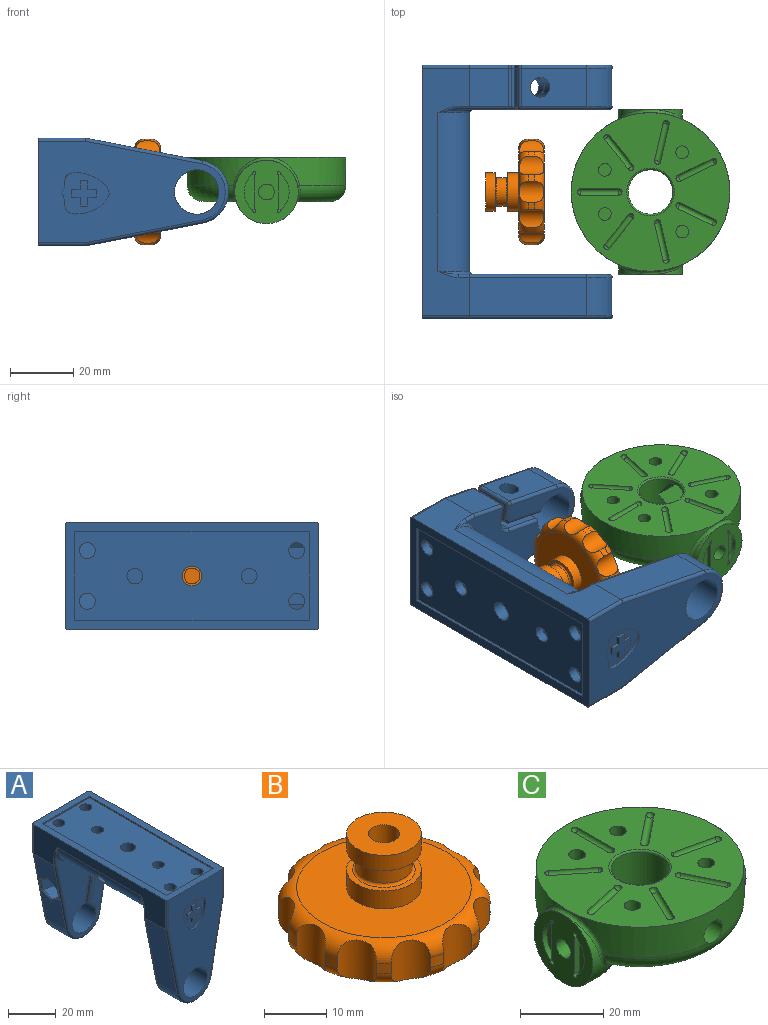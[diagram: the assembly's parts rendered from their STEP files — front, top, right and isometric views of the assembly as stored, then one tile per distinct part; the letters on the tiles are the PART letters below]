
ASSEMBLY  parts=3 mates=2
PART A: 167 faces, bbox 39.4x80x60.8 mm
  f0: plane 59x32mm, normal (0,-1,0), area 1187mm2, adj f6,f16,f97,f98,f99,f100,f101,f162
  f1: plane 36.91x12mm, normal (-0.98,0,-0.19), area 346.3mm2, adj f17,f18,f86,f104,f129,f130,f131,f132
  f2: plane 74x0.7mm, normal (-1,0,0), area 51.8mm2, adj f3,f5,f6,f35
  f3: plane 28x0.7mm, normal (0,1,0), area 19.6mm2, adj f2,f4,f6,f35
  f4: plane 74x0.7mm, normal (1,0,0), area 51.8mm2, adj f3,f5,f6,f35
  f5: plane 28x0.7mm, normal (0,-1,0), area 19.6mm2, adj f2,f4,f6,f35
  f6: plane 80x34mm, normal (0,0,1), area 647.1mm2, adj f0,f2,f3,f4,f5,f17,f19,f20
  f7: cylinder r=3.1mm len=6.2mm, axis (0,0,-1), area 83.8mm2, adj f31,f35
  f8: cylinder r=6.1mm len=12.2mm, axis (0,0,-1), area 378.3mm2, adj f22,f31,f32
  f9: plane 20.61x12mm, normal (0.98,0,-0.19), area 221.8mm2, adj f18,f29,f88,f107,f108
  f10: plane 12.37x12mm, normal (0.98,0,-0.19), area 151.2mm2, adj f19,f93,f123,f126
  f11: cylinder r=7mm len=14mm, axis (0,1,0), area 586.5mm2, adj f12,f20,f25,f28,f91,f96,f112,f120
  f12: plane 47.68x32mm, normal (0,-1,0), area 755.3mm2, adj f11,f79,f80,f81,f103,f104,f106,f108
  f13: plane 36.91x12mm, normal (-0.98,0,-0.19), area 451.2mm2, adj f14,f17,f98,f115
  f14: cylinder r=10mm len=19.63mm, axis (0,1,0), area 330.9mm2, adj f13,f15,f100,f117
  f15: plane 36.91x12mm, normal (0.98,0,-0.19), area 451.2mm2, adj f14,f19,f101,f119
  f16: cylinder r=7mm len=14mm, axis (0,1,0), area 615.8mm2, adj f0,f21
  f17: plane 78x15mm, normal (-1,0,0), area 639.6mm2, adj f1,f6,f13,f74,f85,f97,f102,f103
  f18: cylinder r=10mm len=19.63mm, axis (0,1,0), area 330.9mm2, adj f1,f9,f87,f106
  f19: plane 78x15mm, normal (1,0,0), area 639.6mm2, adj f6,f10,f15,f73,f92,f99,f116,f118
  f20: plane 59x32mm, normal (0,1,0), area 1095.5mm2, adj f6,f11,f85,f86,f87,f88,f89,f90
  f21: plane 47.68x32mm, normal (0,1,0), area 846.9mm2, adj f16,f82,f83,f84,f114,f115,f117,f118
  f22: plane 50x14mm, normal (0,0,-1), area 583.1mm2, adj f8,f73,f74,f80,f83
  f23: plane 12x4.91mm, normal (-0.19,0,-0.98), area 60mm2, adj f24,f94,f123,f124
  f24: cylinder r=4mm len=12mm, axis (0,1,0), area 75.4mm2, adj f23,f25,f95,f122
  f25: plane 12.76x12mm, normal (0.98,0,-0.19), area 125.8mm2, adj f11,f24,f30,f96,f120
  f26: cylinder r=2mm len=12mm, axis (0,1,0), area 37.7mm2, adj f27,f28,f90,f111
  f27: plane 12x4.91mm, normal (0.19,0,0.98), area 60mm2, adj f26,f89,f107,f110
  f28: plane 13.05x12mm, normal (-0.98,0,0.19), area 129.3mm2, adj f11,f26,f29,f91,f112
  f29: cylinder r=3.1mm len=9.04mm, axis (0.98,0,-0.19), area 155.8mm2, adj f9,f28
  f30: cylinder r=3.1mm len=9.04mm, axis (0.98,0,-0.19), area 155.8mm2, adj f25,f72
  f31: plane 12.2x12.2mm, normal (0,0,-1), area 86.7mm2, adj f7,f8
  f32: cylinder r=1.25mm len=4.03mm, axis (-1,0,0), area 31.1mm2, adj f8,f33
  f33: plane 6x6mm, normal (-1,0,0), area 23.4mm2, adj f32,f34
  f34: cylinder r=3mm len=6.8mm, axis (-1,0,0), area 99.7mm2, adj f33,f74
  f35: plane 74x28mm, normal (0,0,1), area 1924mm2, adj f2,f3,f4,f5,f7,f36,f37,f38
  f36: cylinder r=2.5mm len=5mm, axis (0,0,1), area 47.1mm2, adj f35,f39
  f37: cylinder r=2.5mm len=5mm, axis (0,0,1), area 47.1mm2, adj f35,f39
  f38: cylinder r=2.5mm len=5mm, axis (0,0,1), area 47.1mm2, adj f35,f39
  f39: plane 35.5x28mm, normal (0,0,-1), area 808mm2, adj f36,f37,f38,f45,f46,f47,f48,f49
  f40: plane 9.85x8mm, normal (-0.98,0,0.19), area 80.2mm2, adj f41,f43,f48,f49
  f41: plane 25.12x8mm, normal (0.19,0,0.98), area 204.7mm2, adj f40,f42,f43,f48
  f42: plane 8x4.96mm, normal (0.98,0,0.19), area 40.4mm2, adj f41,f43,f47,f48
  f43: plane 28x19.85mm, normal (0,1,0), area 302.8mm2, adj f40,f41,f42,f44,f47,f49,f77,f78
  f44: plane 23.34x14mm, normal (0,0,1), area 294.2mm2, adj f43,f45,f46,f77,f78
  f45: plane 8.3x7.29mm, normal (0,1,0), area 50mm2, adj f39,f44,f46,f47,f78
  f46: cylinder r=9mm len=15.58mm, axis (0,0,1), area 167.1mm2, adj f39,f44,f45,f50,f77
  f47: plane 31x11.3mm, normal (1,0,0), area 120.3mm2, adj f39,f42,f43,f45,f48,f78
  f48: plane 28x21.15mm, normal (0,-1,0), area 514.1mm2, adj f39,f40,f41,f42,f47,f49
  f49: plane 35.5x11.3mm, normal (-1,0,0), area 126.2mm2, adj f39,f40,f43,f48,f50,f77
  f50: plane 8.04x5.13mm, normal (0,1,0), area 32.2mm2, adj f39,f46,f49,f77
  f51: cylinder r=2.5mm len=5mm, axis (0,0,1), area 47.1mm2, adj f35,f54
  f52: cylinder r=2.5mm len=5mm, axis (0,0,1), area 47.1mm2, adj f35,f54
  f53: cylinder r=2.5mm len=5mm, axis (0,0,1), area 47.1mm2, adj f35,f54
  f54: plane 35.5x28mm, normal (0,0,-1), area 808mm2, adj f51,f52,f53,f60,f61,f62,f63,f64
  f55: plane 35x28mm, normal (0,-1,0), area 683.4mm2, adj f56,f57,f58,f59,f64,f65,f75,f76
  f56: plane 25x8mm, normal (0.98,0,0.19), area 203.8mm2, adj f55,f57,f60,f64
  f57: plane 18.27x8mm, normal (0,0,1), area 146.1mm2, adj f55,f56,f58,f60
  f58: plane 25x8mm, normal (-0.98,0,0.19), area 203.8mm2, adj f55,f57,f60,f65
  f59: plane 23.34x14mm, normal (0,0,1), area 294.2mm2, adj f55,f61,f62,f75,f76
  f60: plane 36.3x28mm, normal (0,1,0), area 894.8mm2, adj f54,f56,f57,f58,f64,f65
  f61: plane 8.3x7.29mm, normal (0,-1,0), area 50mm2, adj f54,f59,f62,f64,f76
  f62: cylinder r=9mm len=15.58mm, axis (0,0,1), area 167.1mm2, adj f54,f59,f61,f63,f75
  f63: plane 8.04x5.13mm, normal (0,-1,0), area 32.2mm2, adj f54,f62,f65,f75
  f64: plane 31x11.3mm, normal (1,0,0), area 120.3mm2, adj f54,f55,f56,f60,f61,f76
  f65: plane 35.5x11.3mm, normal (-1,0,0), area 126.1mm2, adj f54,f55,f58,f60,f63,f75
  f66: plane 10.55x4.84mm, normal (-0.17,0.5,-0.85), area 56.4mm2, adj f67,f71,f72,f132,f134
  f67: plane 9.27x7.25mm, normal (0,1,0), area 46.1mm2, adj f66,f68,f72,f130,f132
  f68: plane 6.89x4.8mm, normal (0.17,0.5,0.85), area 35.8mm2, adj f67,f69,f72,f130
  f69: plane 6.89x4.8mm, normal (0.17,-0.5,0.85), area 35.8mm2, adj f68,f70,f72,f129
  f70: plane 9.27x7.25mm, normal (0,-1,0), area 46.1mm2, adj f69,f71,f72,f129,f131
  f71: plane 10.55x4.84mm, normal (-0.17,-0.5,-0.85), area 56.4mm2, adj f66,f70,f72,f131,f133
  f72: plane 10.88x9.6mm, normal (-0.98,0,0.19), area 49.6mm2, adj f30,f66,f67,f68,f69,f70,f71
  f73: cylinder r=10mm len=50mm, axis (0,-1,0), area 785.4mm2, adj f19,f22,f81,f84
  f74: cylinder r=10mm len=50mm, axis (0,1,0), area 751.6mm2, adj f17,f22,f34,f79,f82
  f75: cylinder r=7mm len=27.5mm, axis (0,1,0), area 297.6mm2, adj f55,f59,f62,f63,f65
  f76: cylinder r=7mm len=23mm, axis (0,-1,0), area 252.9mm2, adj f55,f59,f61,f64
  f77: cylinder r=7mm len=27.5mm, axis (0,1,0), area 297.6mm2, adj f43,f44,f46,f49,f50
  f78: cylinder r=7mm len=23mm, axis (0,-1,0), area 252.9mm2, adj f43,f44,f45,f47
  f79: torus R=11mm, axis (0,1,0), area 20mm2, adj f12,f74,f80,f102
  f80: cylinder r=1mm len=14mm, axis (1,0,0), area 22mm2, adj f12,f22,f79,f81
  f81: torus R=11mm, axis (0,1,0), area 20mm2, adj f12,f73,f80,f128
  f82: torus R=11mm, axis (0,1,0), area 20mm2, adj f21,f74,f83,f113
  f83: cylinder r=1mm len=14mm, axis (-1,0,0), area 22mm2, adj f21,f22,f82,f84
  f84: torus R=11mm, axis (0,1,0), area 20mm2, adj f21,f73,f83,f116
  f85: cylinder r=1mm len=15mm, axis (0,0,-1), area 23.5mm2, adj f6,f17,f20,f86
  f86: cylinder r=1mm len=37.1mm, axis (0.19,0,-0.98), area 59mm2, adj f1,f20,f85,f87
  f87: torus R=9mm, axis (0,-1,0), area 41.7mm2, adj f18,f20,f86,f88
  f88: cylinder r=1mm len=20.8mm, axis (0.19,0,0.98), area 33mm2, adj f9,f20,f87,f105
  f89: cylinder r=1mm len=5.1mm, axis (-0.98,0,0.19), area 7.9mm2, adj f20,f27,f90,f105
  f90: torus R=1mm, axis (0,-1,0), area 4mm2, adj f20,f26,f89,f91
  f91: cylinder r=1mm len=13.61mm, axis (-0.19,0,-0.98), area 21.1mm2, adj f11,f20,f28,f90
  f92: cylinder r=1mm len=15mm, axis (0,0,1), area 23.5mm2, adj f6,f19,f20,f93
  f93: cylinder r=1mm len=12.56mm, axis (0.19,0,0.98), area 19.7mm2, adj f10,f20,f92,f121
  f94: cylinder r=1mm len=5.1mm, axis (0.98,0,-0.19), area 7.9mm2, adj f20,f23,f95,f121
  f95: torus R=5mm, axis (0,-1,0), area 10.8mm2, adj f20,f24,f94,f96
  f96: cylinder r=1mm len=13.02mm, axis (0.19,0,0.98), area 20.5mm2, adj f11,f20,f25,f95
  f97: cylinder r=1mm len=15mm, axis (0,0,1), area 23.5mm2, adj f0,f6,f17,f98
  f98: cylinder r=1mm len=37.1mm, axis (-0.19,0,0.98), area 59mm2, adj f0,f13,f97,f100
  f99: cylinder r=1mm len=15mm, axis (0,0,-1), area 23.5mm2, adj f0,f6,f19,f101
  f100: torus R=9mm, axis (0,-1,0), area 41.7mm2, adj f0,f14,f98,f101
  f101: cylinder r=1mm len=37.1mm, axis (-0.19,0,-0.98), area 59mm2, adj f0,f15,f99,f100
  f102: bspline ~6.59x2mm, area 5mm2, adj f17,f79,f103
  f103: cylinder r=1mm len=3.68mm, axis (0,0,1), area 5.7mm2, adj f12,f17,f102,f104
  f104: cylinder r=1mm len=37.1mm, axis (-0.19,0,0.98), area 59mm2, adj f1,f12,f103,f106
  f105: sphere r=1mm, area 1.5mm2, adj f88,f89,f107
  f106: torus R=9mm, axis (0,1,0), area 41.7mm2, adj f12,f18,f104,f108
  f107: cylinder r=1mm len=12mm, axis (0,-1,0), area 18.8mm2, adj f9,f27,f105,f109
  f108: cylinder r=1mm len=20.8mm, axis (-0.19,0,-0.98), area 33mm2, adj f9,f12,f106,f109
  f109: sphere r=1mm, area 1.6mm2, adj f107,f108,f110
  f110: cylinder r=1mm len=5.1mm, axis (-0.98,0,0.19), area 7.9mm2, adj f12,f27,f109,f111
  f111: torus R=1mm, axis (0,1,0), area 4mm2, adj f12,f26,f110,f112
  f112: cylinder r=1mm len=13.61mm, axis (-0.19,0,-0.98), area 21.1mm2, adj f11,f12,f28,f111
  f113: bspline ~6.59x2mm, area 5mm2, adj f17,f82,f114
  f114: cylinder r=1mm len=3.68mm, axis (0,0,1), area 5.7mm2, adj f17,f21,f113,f115
  f115: cylinder r=1mm len=37.1mm, axis (0.19,0,-0.98), area 59mm2, adj f13,f21,f114,f117
  f116: bspline ~6.59x2mm, area 5mm2, adj f19,f84,f118
  f117: torus R=9mm, axis (0,1,0), area 41.7mm2, adj f14,f21,f115,f119
  f118: cylinder r=1mm len=3.68mm, axis (0,0,1), area 5.7mm2, adj f19,f21,f116,f119
  f119: cylinder r=1mm len=37.1mm, axis (0.19,0,0.98), area 59mm2, adj f15,f21,f117,f118
  f120: cylinder r=1mm len=13.02mm, axis (0.19,0,0.98), area 20.5mm2, adj f11,f12,f25,f122
  f121: sphere r=1mm, area 1.6mm2, adj f93,f94,f123
  f122: torus R=5mm, axis (0,1,0), area 10.8mm2, adj f12,f24,f120,f124
  f123: cylinder r=1mm len=12mm, axis (0,1,0), area 18.8mm2, adj f10,f23,f121,f125
  f124: cylinder r=1mm len=5.1mm, axis (0.98,0,-0.19), area 7.9mm2, adj f12,f23,f122,f125
  f125: sphere r=1mm, area 1.6mm2, adj f123,f124,f126
  f126: cylinder r=1mm len=12.56mm, axis (-0.19,0,-0.98), area 19.7mm2, adj f10,f12,f125,f127
  f127: cylinder r=1mm len=3.68mm, axis (0,0,1), area 5.7mm2, adj f12,f19,f126,f128
  f128: bspline ~6.59x2mm, area 5mm2, adj f19,f81,f127
  f129: cylinder r=0.5mm len=5.56mm, axis (-0.1,0.85,0.52), area 5.6mm2, adj f1,f69,f70,f130,f131
  f130: cylinder r=0.5mm len=5.56mm, axis (0.1,0.85,-0.52), area 5.6mm2, adj f1,f67,f68,f129,f132
  f131: cylinder r=0.5mm len=6.58mm, axis (-0.19,0,0.98), area 4.9mm2, adj f1,f70,f71,f129,f133
  f132: cylinder r=0.5mm len=6.58mm, axis (0.19,0,-0.98), area 4.9mm2, adj f1,f66,f67,f130,f134
  f133: cylinder r=0.5mm len=5.55mm, axis (-0.1,-0.85,0.52), area 3.7mm2, adj f1,f71,f131,f134
  f134: cylinder r=0.5mm len=5.55mm, axis (0.1,-0.85,-0.52), area 3.7mm2, adj f1,f66,f132,f133
  f135: extruded ~15.03x6.52mm, area 22.3mm2, adj f20,f148,f149
  f136: plane 2.8x1mm, normal (-1,0,0), area 2.8mm2, adj f137,f147,f149,f150
  f137: plane 2.4x1mm, normal (0,0,-1), area 2.4mm2, adj f136,f138,f149,f150
  f138: plane 2.8x1mm, normal (1,0,0), area 2.8mm2, adj f137,f139,f149,f150
  f139: plane 2.8x1mm, normal (0,0,-1), area 2.8mm2, adj f138,f140,f149,f150
  f140: plane 2.4x1mm, normal (1,0,0), area 2.4mm2, adj f139,f141,f149,f150
  f141: plane 2.8x1mm, normal (0,0,1), area 2.8mm2, adj f140,f142,f149,f150
  f142: plane 2.8x1mm, normal (1,0,0), area 2.8mm2, adj f141,f143,f149,f150
  f143: plane 2.4x1mm, normal (0,0,1), area 2.4mm2, adj f142,f144,f149,f150
  f144: plane 2.8x1mm, normal (-1,0,0), area 2.8mm2, adj f143,f145,f149,f150
  f145: plane 2.8x1mm, normal (0,0,1), area 2.8mm2, adj f144,f146,f149,f150
  f146: plane 2.4x1mm, normal (-1,0,0), area 2.4mm2, adj f145,f147,f149,f150
  f147: plane 2.8x1mm, normal (0,0,-1), area 2.8mm2, adj f136,f146,f149,f150
  f148: extruded ~15.03x6.52mm, area 22.3mm2, adj f20,f135,f149
  f149: plane 15.18x13.69mm, normal (0,1,0), area 114.1mm2, adj f135,f136,f137,f138,f139,f140,f141,f142
  f150: plane 8x8mm, normal (0,1,0), area 32.6mm2, adj f136,f137,f138,f139,f140,f141,f142,f143
  f151: plane 2.8x1mm, normal (1,0,0), area 2.8mm2, adj f152,f164,f165,f166
  f152: plane 2.4x1mm, normal (0,0,-1), area 2.4mm2, adj f151,f153,f165,f166
  f153: plane 2.8x1mm, normal (-1,0,0), area 2.8mm2, adj f152,f154,f165,f166
  f154: plane 2.8x1mm, normal (0,0,-1), area 2.8mm2, adj f153,f155,f165,f166
  f155: plane 2.4x1mm, normal (-1,0,0), area 2.4mm2, adj f154,f156,f165,f166
  f156: plane 2.8x1mm, normal (0,0,1), area 2.8mm2, adj f155,f157,f165,f166
  f157: plane 2.8x1mm, normal (-1,0,0), area 2.8mm2, adj f156,f158,f165,f166
  f158: plane 2.4x1mm, normal (0,0,1), area 2.4mm2, adj f157,f159,f165,f166
  f159: plane 2.8x1mm, normal (1,0,0), area 2.8mm2, adj f158,f160,f165,f166
  f160: plane 2.8x1mm, normal (0,0,1), area 2.8mm2, adj f159,f161,f165,f166
  f161: plane 2.4x1mm, normal (1,0,0), area 2.4mm2, adj f160,f164,f165,f166
  f162: extruded ~15.03x6.52mm, area 22.3mm2, adj f0,f163,f165
  f163: extruded ~15.03x6.52mm, area 22.3mm2, adj f0,f162,f165
  f164: plane 2.8x1mm, normal (0,0,-1), area 2.8mm2, adj f151,f161,f165,f166
  f165: plane 15.18x13.69mm, normal (0,-1,0), area 114.1mm2, adj f151,f152,f153,f154,f155,f156,f157,f158
  f166: plane 8x8mm, normal (0,-1,0), area 32.6mm2, adj f151,f152,f153,f154,f155,f156,f157,f158
PART B: 38 faces, bbox 36.8x36.8x18.5 mm
  f0: cylinder r=17mm len=2.26mm, axis (0,0,1), area 4.7mm2, adj f22,f23,f33,f35
  f1: cylinder r=17mm len=2mm, axis (0,0,1), area 4.7mm2, adj f22,f23,f34,f35
  f2: cylinder r=17mm len=2.26mm, axis (0,0,1), area 4.7mm2, adj f22,f23,f32,f33
  f3: cylinder r=17mm len=2mm, axis (0,0,1), area 4.7mm2, adj f22,f23,f31,f32
  f4: cylinder r=17mm len=2.26mm, axis (0,0,1), area 4.7mm2, adj f22,f23,f30,f31
  f5: cylinder r=17mm len=2.26mm, axis (0,0,1), area 4.7mm2, adj f22,f23,f28,f30
  f6: cylinder r=17mm len=2.26mm, axis (0,0,1), area 4.7mm2, adj f22,f23,f25,f29
  f7: cylinder r=17mm len=2mm, axis (0,0,1), area 4.7mm2, adj f22,f23,f28,f29
  f8: cylinder r=17mm len=2.26mm, axis (0,0,1), area 4.7mm2, adj f22,f23,f24,f27
  f9: cylinder r=17mm len=2mm, axis (0,0,1), area 4.7mm2, adj f22,f23,f26,f27
  f10: cylinder r=17mm len=2.26mm, axis (0,0,1), area 4.7mm2, adj f22,f23,f25,f26
  f11: cylinder r=4.5mm len=9mm, axis (0,0,1), area 84.8mm2, adj f36,f37
  f12: plane 12x12mm, normal (0,0,1), area 34.6mm2, adj f13,f36
  f13: cylinder r=6mm len=12mm, axis (0,0,1), area 131.9mm2, adj f12,f14
  f14: plane 28x28mm, normal (0,0,1), area 502.7mm2, adj f13,f22
  f15: cylinder r=17mm len=2.26mm, axis (0,0,1), area 4.7mm2, adj f22,f23,f24,f34
  f16: plane 28x28mm, normal (0,0,-1), area 615.8mm2, adj f23
  f17: plane 5x5mm, normal (0,0,1), area 19.6mm2, adj f18
  f18: cylinder r=2.5mm len=14.5mm, axis (0,0,1), area 227.8mm2, adj f17,f19
  f19: plane 12x12mm, normal (0,0,1), area 93.5mm2, adj f18,f20
  f20: cylinder r=6mm len=12mm, axis (0,0,1), area 113.1mm2, adj f19,f21
  f21: plane 12x12mm, normal (0,0,-1), area 34.6mm2, adj f20,f37
  f22: torus R=14mm, axis (0,0,-1), area 241mm2, adj f0,f1,f2,f3,f4,f5,f6,f7
  f23: torus R=14mm, axis (0,0,1), area 241mm2, adj f0,f1,f2,f3,f4,f5,f6,f7
  f24: cylinder r=4mm len=7.66mm, axis (0,0,1), area 50.6mm2, adj f8,f15,f22,f23
  f25: cylinder r=4mm len=7.66mm, axis (0,0,1), area 50.6mm2, adj f6,f10,f22,f23
  f26: cylinder r=4mm len=7.66mm, axis (0,0,1), area 50.6mm2, adj f9,f10,f22,f23
  f27: cylinder r=4mm len=7.66mm, axis (0,0,1), area 50.6mm2, adj f8,f9,f22,f23
  f28: cylinder r=4mm len=7.66mm, axis (0,0,1), area 50.6mm2, adj f5,f7,f22,f23
  f29: cylinder r=4mm len=7.66mm, axis (0,0,1), area 50.6mm2, adj f6,f7,f22,f23
  f30: cylinder r=4mm len=7.66mm, axis (0,0,1), area 50.6mm2, adj f4,f5,f22,f23
  f31: cylinder r=4mm len=7.66mm, axis (0,0,1), area 50.6mm2, adj f3,f4,f22,f23
  f32: cylinder r=4mm len=7.66mm, axis (0,0,1), area 50.6mm2, adj f2,f3,f22,f23
  f33: cylinder r=4mm len=7.66mm, axis (0,0,1), area 50.6mm2, adj f0,f2,f22,f23
  f34: cylinder r=4mm len=7.66mm, axis (0,0,1), area 50.6mm2, adj f1,f15,f22,f23
  f35: cylinder r=4mm len=7.66mm, axis (0,0,1), area 50.6mm2, adj f0,f1,f22,f23
  f36: torus R=5mm, axis (0,0,1), area 23.1mm2, adj f11,f12
  f37: torus R=5mm, axis (0,0,-1), area 23.1mm2, adj f11,f21
PART C: 126 faces, bbox 52.2x54.3x21.2 mm
  f0: sphere r=1mm, area 3.1mm2, adj f1,f61
  f1: cylinder r=1mm len=10.63mm, axis (0.78,-0.62,0), area 37.7mm2, adj f0,f2,f61
  f2: sphere r=1mm, area 3.1mm2, adj f1,f61
  f3: sphere r=1mm, area 3.1mm2, adj f4,f61
  f4: cylinder r=1mm len=12.14mm, axis (0.97,0.22,0), area 37.7mm2, adj f3,f5,f61
  f5: sphere r=1mm, area 3.1mm2, adj f4,f61
  f6: sphere r=1mm, area 3.1mm2, adj f7,f61
  f7: cylinder r=1mm len=11.68mm, axis (0.43,0.9,0), area 37.7mm2, adj f6,f8,f61
  f8: sphere r=1mm, area 3.1mm2, adj f7,f61
  f9: sphere r=1mm, area 3.1mm2, adj f10,f61
  f10: cylinder r=1mm len=11.68mm, axis (-0.43,0.9,0), area 37.7mm2, adj f9,f11,f61
  f11: sphere r=1mm, area 3.1mm2, adj f10,f61
  f12: sphere r=1mm, area 3.1mm2, adj f13,f61
  f13: cylinder r=1mm len=12.14mm, axis (-0.97,0.22,0), area 37.7mm2, adj f12,f14,f61
  f14: sphere r=1mm, area 3.1mm2, adj f13,f61
  f15: sphere r=1mm, area 3.1mm2, adj f16,f61
  f16: cylinder r=1mm len=10.63mm, axis (-0.78,-0.62,0), area 37.7mm2, adj f15,f17,f61
  f17: sphere r=1mm, area 3.1mm2, adj f16,f61
  f18: sphere r=10mm, area 71.2mm2, adj f24,f30,f33,f39,f41,f77,f118
  f19: sphere r=10mm, area 71.2mm2, adj f22,f30,f34,f50,f54,f78,f118
  f20: sphere r=10mm, area 71.2mm2, adj f23,f30,f34,f55,f56,f78,f118
  f21: sphere r=10mm, area 71.2mm2, adj f25,f30,f33,f47,f48,f77,f118
  f22: plane 8x6.86mm, normal (0,1,0), area 27.3mm2, adj f19,f49,f50,f51,f118
  f23: plane 8x6.86mm, normal (0,-1,0), area 27.3mm2, adj f20,f46,f52,f56,f118
  f24: plane 8x6.86mm, normal (0,1,0), area 27.3mm2, adj f18,f38,f39,f40,f118
  f25: plane 8x6.86mm, normal (0,-1,0), area 27.3mm2, adj f21,f45,f48,f53,f118
  f26: plane 15.9x8mm, normal (0.99,-0.16,0), area 115.8mm2, adj f30,f32,f45,f47,f48,f53,f76,f118
  f27: plane 15.9x8mm, normal (-0.99,-0.16,0), area 115.8mm2, adj f30,f32,f46,f52,f55,f56,f75,f118
  f28: plane 12.16x8.09mm, normal (1,0,0), area 85.7mm2, adj f30,f31,f38,f39,f40,f41,f74,f118
  f29: plane 12.16x8.09mm, normal (-1,0,0), area 85.7mm2, adj f30,f31,f49,f50,f51,f54,f74,f118
  f30: cylinder r=22mm len=44mm, axis (0,0,-1), area 656mm2, adj f18,f19,f20,f21,f26,f27,f28,f29
  f31: cylinder r=19mm len=3mm, axis (0,0,1), area 9mm2, adj f28,f29,f74,f118
  f32: cylinder r=19mm len=13.04mm, axis (0,0,1), area 27.3mm2, adj f26,f27,f37,f75,f76,f118
  f33: cylinder r=19mm len=16.03mm, axis (0,0,1), area 42.8mm2, adj f18,f21,f77,f118
  f34: cylinder r=19mm len=16.03mm, axis (0,0,1), area 42.8mm2, adj f19,f20,f78,f118
  f35: plane 20x20mm, normal (1,0,0), area 238.4mm2, adj f66,f67,f91,f92,f93,f94,f96,f97
  f36: cylinder r=25mm len=50mm, axis (0,0,-1), area 534.1mm2, adj f37,f43,f61,f84,f90
  f37: cylinder r=3.1mm len=8.5mm, axis (0,1,0), area 136.6mm2, adj f30,f32,f36,f43,f75,f76,f117
  f38: torus R=12mm, axis (0,0,-1), area 35.4mm2, adj f24,f28,f39,f40
  f39: plane 16.07x15.94mm, normal (0,0,1), area 127.7mm2, adj f18,f24,f28,f38,f41
  f40: cylinder r=10mm len=7.67mm, axis (0,0,-1), area 60.5mm2, adj f24,f28,f38,f118
  f41: torus R=20mm, axis (0,0,-1), area 68.2mm2, adj f18,f28,f30,f39
  f42: cylinder r=25mm len=50mm, axis (0,0,-1), area 563.1mm2, adj f57,f61,f84,f90
  f43: torus R=20mm, axis (0,0,-1), area 401.8mm2, adj f36,f37,f58,f80,f82,f86,f88
  f44: cylinder r=7mm len=14mm, axis (0,0,-1), area 428.4mm2, adj f72,f73,f111,f112,f113,f114,f115,f116
  f45: torus R=12mm, axis (0,0,-1), area 10.2mm2, adj f25,f26,f48,f53
  f46: cylinder r=10mm len=6mm, axis (0,0,-1), area 8.6mm2, adj f23,f27,f52,f118
  f47: torus R=20mm, axis (0,0,-1), area 53.5mm2, adj f21,f26,f30,f48
  f48: plane 14.97x11.22mm, normal (0,0,1), area 80.6mm2, adj f21,f25,f26,f45,f47
  f49: torus R=12mm, axis (0,0,-1), area 35.4mm2, adj f22,f29,f50,f51
  f50: plane 16.07x15.94mm, normal (0,0,1), area 127.7mm2, adj f19,f22,f29,f49,f54
  f51: cylinder r=10mm len=7.67mm, axis (0,0,-1), area 60.5mm2, adj f22,f29,f49,f118
  f52: torus R=12mm, axis (0,0,-1), area 10.2mm2, adj f23,f27,f46,f56
  f53: cylinder r=10mm len=6mm, axis (0,0,-1), area 8.6mm2, adj f25,f26,f45,f118
  f54: torus R=20mm, axis (0,0,-1), area 68.2mm2, adj f19,f29,f30,f50
  f55: torus R=20mm, axis (0,0,-1), area 53.5mm2, adj f20,f27,f30,f56
  f56: plane 14.97x11.22mm, normal (0,0,1), area 80.6mm2, adj f20,f23,f27,f52,f55
  f57: torus R=20mm, axis (0,0,-1), area 403mm2, adj f42,f58,f81,f83,f87,f89
  f58: plane 40x34.89mm, normal (0,0,-1), area 668.4mm2, adj f43,f57,f71,f79,f85
  f59: cylinder r=9.5mm len=19mm, axis (0,0,-1), area 41.8mm2, adj f60,f71
  f60: plane 19x19mm, normal (0,0,-1), area 106.8mm2, adj f59,f72
  f61: plane 50x50mm, normal (0,0,1), area 1546.5mm2, adj f0,f1,f2,f3,f4,f5,f6,f7
  f62: cylinder r=10mm len=20mm, axis (1,0,0), area 201.5mm2, adj f63,f64,f88,f89,f90
  f63: sphere r=10mm, area 201.4mm2, adj f62,f85,f86,f87
  f64: plane 20x20mm, normal (-1,0,0), area 238.4mm2, adj f62,f69,f101,f102,f103,f104,f106,f107
  f65: sphere r=10mm, area 201.4mm2, adj f66,f79,f80,f81
  f66: cylinder r=10mm len=20mm, axis (1,0,0), area 201.5mm2, adj f35,f65,f82,f83,f84
  f67: cylinder r=2.5mm len=13mm, axis (1,0,0), area 204.2mm2, adj f35,f68
  f68: plane 5x5mm, normal (1,0,0), area 19.6mm2, adj f67
  f69: cylinder r=2.5mm len=13mm, axis (-1,0,0), area 204.2mm2, adj f64,f70
  f70: plane 5x5mm, normal (-1,0,0), area 19.6mm2, adj f69
  f71: torus R=10mm, axis (0,0,-1), area 47.8mm2, adj f58,f59
  f72: torus R=7.5mm, axis (0,0,-1), area 35.4mm2, adj f44,f60
  f73: torus R=7.5mm, axis (0,0,-1), area 35.4mm2, adj f44,f61
  f74: plane 3.06x3mm, normal (0,0,1), area 9mm2, adj f28,f29,f30,f31
  f75: plane 3.94x3.45mm, normal (0,0,1), area 9.8mm2, adj f27,f30,f32,f37
  f76: plane 3.94x3.45mm, normal (0,0,1), area 9.8mm2, adj f26,f30,f32,f37
  f77: plane 17.46x4.92mm, normal (0,0,1), area 52.1mm2, adj f18,f21,f30,f33
  f78: plane 17.46x4.92mm, normal (0,0,1), area 52.1mm2, adj f19,f20,f30,f34
  f79: torus R=10.25mm, axis (0,0,-1), area 29.5mm2, adj f58,f65,f80,f81
  f80: bspline ~5.18x2.02mm, area 3.2mm2, adj f43,f65,f79,f82
  f81: bspline ~4.38x2.02mm, area 3.2mm2, adj f57,f65,f79,f83
  f82: bspline ~5.68x4.74mm, area 6.2mm2, adj f43,f66,f80,f84
  f83: bspline ~6.52x4.74mm, area 6.2mm2, adj f57,f66,f81,f84
  f84: bspline ~21.18x11.28mm, area 39.9mm2, adj f36,f42,f66,f82,f83
  f85: torus R=10.25mm, axis (0,0,-1), area 29.5mm2, adj f58,f63,f86,f87
  f86: bspline ~4.38x2.02mm, area 3.2mm2, adj f43,f63,f85,f88
  f87: bspline ~5.18x2.02mm, area 3.2mm2, adj f57,f63,f85,f89
  f88: bspline ~6.52x4.74mm, area 6.2mm2, adj f43,f62,f86,f90
  f89: bspline ~5.68x4.74mm, area 6.2mm2, adj f57,f62,f87,f90
  f90: bspline ~21.18x11.28mm, area 39.9mm2, adj f36,f42,f62,f88,f89
  f91: cylinder r=7.1mm len=11.29mm, axis (1,0,0), area 19.6mm2, adj f35,f92,f94,f95
  f92: cylinder r=0.5mm len=1.5mm, axis (1,0,0), area 4mm2, adj f35,f91,f93,f95
  f93: plane 10.87x1.5mm, normal (0,1,0), area 16.3mm2, adj f35,f92,f94,f95
  f94: cylinder r=0.5mm len=1.5mm, axis (1,0,0), area 4mm2, adj f35,f91,f93,f95
  f95: plane 12.87x3.7mm, normal (1,0,0), area 28.1mm2, adj f91,f92,f93,f94
  f96: cylinder r=0.5mm len=1.5mm, axis (1,0,0), area 4mm2, adj f35,f97,f99,f100
  f97: cylinder r=7.1mm len=11.29mm, axis (1,0,0), area 19.6mm2, adj f35,f96,f98,f100
  f98: cylinder r=0.5mm len=1.5mm, axis (1,0,0), area 4mm2, adj f35,f97,f99,f100
  f99: plane 10.87x1.5mm, normal (0,-1,0), area 16.3mm2, adj f35,f96,f98,f100
  f100: plane 12.87x3.7mm, normal (1,0,0), area 28.1mm2, adj f96,f97,f98,f99
  f101: cylinder r=0.5mm len=1.5mm, axis (-1,0,0), area 4mm2, adj f64,f102,f104,f105
  f102: plane 10.87x1.5mm, normal (0,1,0), area 16.3mm2, adj f64,f101,f103,f105
  f103: cylinder r=0.5mm len=1.5mm, axis (-1,0,0), area 4mm2, adj f64,f102,f104,f105
  f104: cylinder r=7.1mm len=11.29mm, axis (-1,0,0), area 19.6mm2, adj f64,f101,f103,f105
  f105: plane 12.87x3.7mm, normal (-1,0,0), area 28.1mm2, adj f101,f102,f103,f104
  f106: plane 10.87x1.5mm, normal (0,-1,0), area 16.3mm2, adj f64,f107,f109,f110
  f107: cylinder r=0.5mm len=1.5mm, axis (-1,0,0), area 4mm2, adj f64,f106,f108,f110
  f108: cylinder r=7.1mm len=11.29mm, axis (-1,0,0), area 19.6mm2, adj f64,f107,f109,f110
  f109: cylinder r=0.5mm len=1.5mm, axis (-1,0,0), area 4mm2, adj f64,f106,f108,f110
  f110: plane 12.87x3.7mm, normal (-1,0,0), area 28.1mm2, adj f106,f107,f108,f109
  f111: plane 10.1x5.66mm, normal (0,0,1), area 54.9mm2, adj f44,f112,f116,f117
  f112: plane 12.38x4.9mm, normal (-0.87,0,0.5), area 62.4mm2, adj f44,f111,f113,f117
  f113: plane 12.38x4.9mm, normal (-0.87,0,-0.5), area 62.4mm2, adj f44,f112,f114,f117
  f114: plane 10.1x5.66mm, normal (0,0,-1), area 54.9mm2, adj f44,f113,f115,f117
  f115: plane 12.38x4.9mm, normal (0.87,0,-0.5), area 62.4mm2, adj f44,f114,f116,f117
  f116: plane 12.38x4.9mm, normal (0.87,0,0.5), area 62.4mm2, adj f44,f111,f115,f117
  f117: plane 11.32x9.8mm, normal (0,1,0), area 53mm2, adj f37,f111,f112,f113,f114,f115,f116
  f118: plane 44x44mm, normal (0,0,-1), area 831.8mm2, adj f18,f19,f20,f21,f22,f23,f24,f25
  f119: sphere r=1mm, area 3.1mm2, adj f61,f120
  f120: cylinder r=1mm len=12mm, axis (0,-1,0), area 37.7mm2, adj f61,f119,f121
  f121: sphere r=1mm, area 3.1mm2, adj f61,f120
  f122: cylinder r=2mm len=4mm, axis (0,0,1), area 37.7mm2, adj f61,f118
  f123: cylinder r=2mm len=4mm, axis (0,0,1), area 37.7mm2, adj f61,f118
  f124: cylinder r=2mm len=4mm, axis (0,0,1), area 37.7mm2, adj f61,f118
  f125: cylinder r=2mm len=4mm, axis (0,0,1), area 37.7mm2, adj f61,f118
PLACE A rot(axis=(0,-1,0),90deg) t=(50,40,17)mm
PLACE B rot(axis=(-0.58,-0.58,0.58),120deg) t=(38.5,0,17)mm
PLACE C rot(axis=(0,0,1),90deg) t=(72,0,11.34)mm
MATE fastened B.f0 <-> A.f7  axis (-1,0,0) through (20,0,17)mm
MATE fastened A.f11 <-> C.f64  axis (0,1,0) through (50,-26,17)mm
